# Revit family: LIXIL - KM2-100 N - COBRA PILLAR TAP METERING
name_source: partatom
category: Plumbing Fixtures
units: mm (PartAtom-declared; Revit-internal decimal feet)

## family parameters
Always vertical = Yes
Cut with Voids When Loaded = No
Enable Cutting in Views = No
Maintain Annotation Orientation = No
OmniClass Number = 23.45.00.00
OmniClass Title = Sanitary, Laundry, and Cleaning Equipment
Part Type = Normal
Room Calculation Point = No
Round Connector Dimension = Use Diameter
Shared = Yes
Work Plane-Based = No

## types (1)
- KM2-100 N
    Default Elevation = 0 mm  [stored 0 ft]
    Description = Cobra mixer to detail and spec. See sanware schedule. Available from Lixil.
    Hosted on lixil.co.za = https://www.lixil.co.za
    M _ MIXER BODY = M _ LIXIL - CHROME 01
    M _ MIXER INDICATOR 01 = M _ LIXIL - PLASTIC - BLUE 01
    M _ MIXER INDICATOR 02 = M _ LIXIL - CHROME 01
    M _ MIXER LEVER = M _ LIXIL - CHROME 01
    M _ MIXER RUBBER = M _ LIXIL - RUBBER - BLACK 01
    Product Specification = Supplier: Lixil.
Product description: Non hold open, self closing. 1/2BSP male iron connection end. 
Product Code: FPT2A1M2-0GT01.
SKU Code: KM2-100/N.
Barcode: 6002194032724.
Brand: Cobra
Range: Cobra.
Category: Plumbing Supplies
Sub-Category: Public Taps
Colour: Brushed Chrome
Package Height: 50 mm
Package Width: 170 mm
Package Length: 220 mm
Package Volume: 1870000 mm³

Notes:
- Refer to manufacturer's and supplier's installation, maintenance and cleaning manual.
- Refer to manufacturer's and supplier's guarantees and warrantees document.

note: [stored X ft] marks values corroborated as IEEE doubles in the binary element streams (Revit-internal decimal feet)

## geometry (parser evidence)
native form markers: Sweep x10
no freeform markers — native parametric forms only
